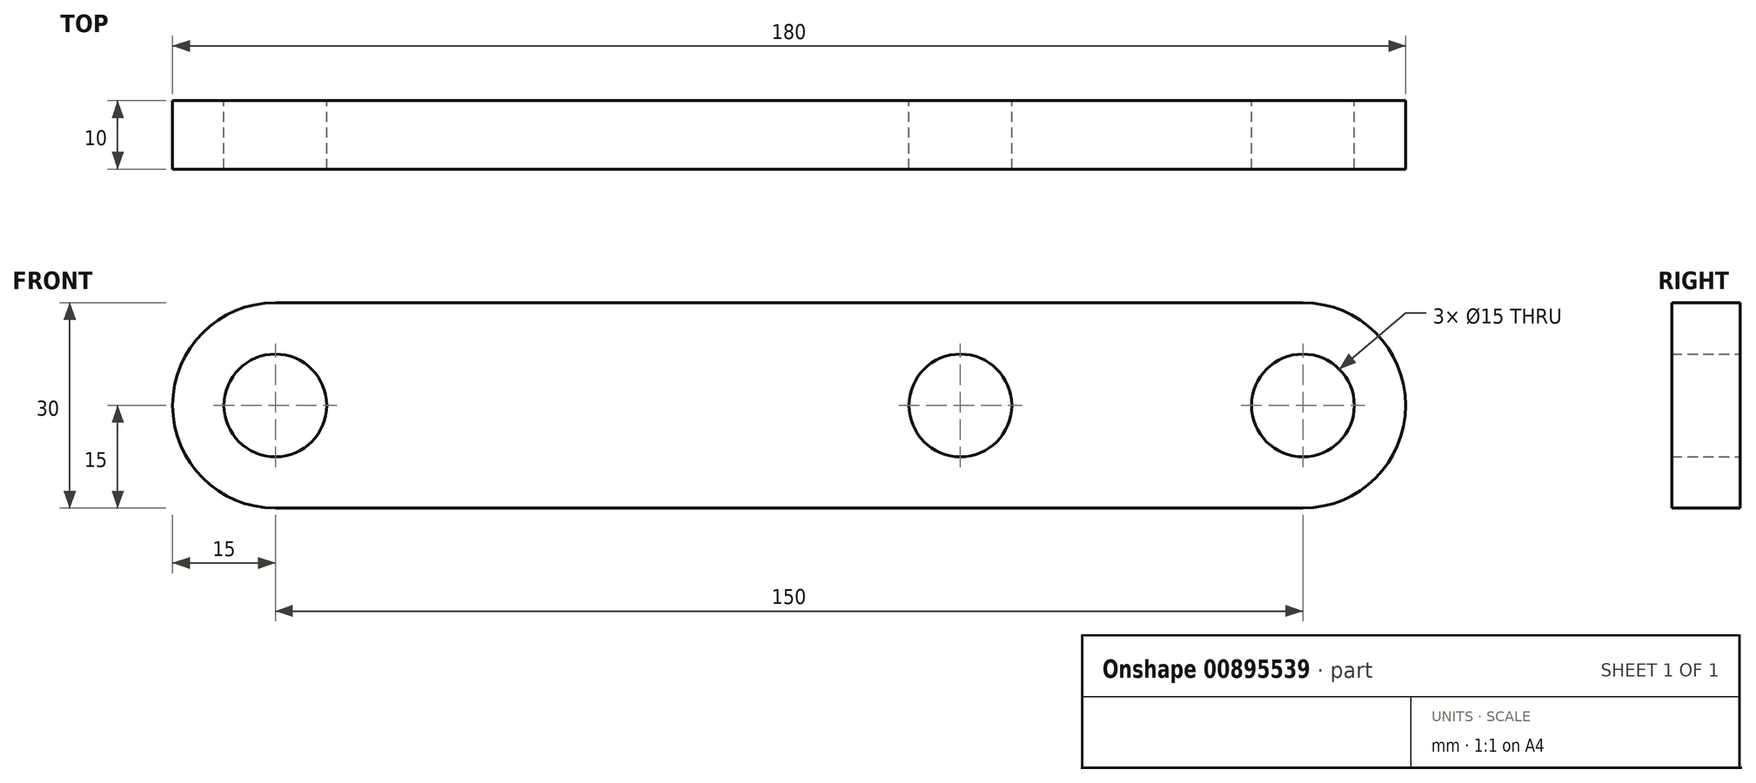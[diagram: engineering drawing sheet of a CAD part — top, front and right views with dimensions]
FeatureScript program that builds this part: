
annotation { "Feature Type Name" : "Feature", "Feature Type Description" : "" }
export const myFeature = defineFeature(function(context is Context, id is Id, definition is map)
    precondition{}
    {
        {
            var Q0;
            Q0=qCreatedBy(makeId("Front.planeOp"),FACE);
            var sketch = newSketch(context, id + "F0", { "sketchPlane" : qUnion([Q0])});
            skCircle(sketch, "E0", {"center": v(0, 0) * mm, "radius": 7.5 * mm});
            skArc(sketch, "E1", {"start": v(0, 15) * mm, "mid": v(-15, 0) * mm, "end": v(0, -15) * mm});
            skCircle(sketch, "E2", {"center": v(150, 0) * mm, "radius": 7.5 * mm});
            skArc(sketch, "E3", {"start": v(150, -15) * mm, "mid": v(165, 0) * mm, "end": v(150, 15) * mm});
            skLineSegment(sketch, "E4", {"start": v(0, 15) * mm, "end": v(150, 15) * mm});
            skLineSegment(sketch, "E5", {"start": v(0, -15) * mm, "end": v(150, -15) * mm});
            skCircle(sketch, "E6", {"center": v(100, 0) * mm, "radius": 7.5 * mm});
            skSolve(sketch);
        }
        {
            var Q0;
            Q0=makeQuery(id+"F0.imprint","IMPRINT",FACE,{"disambiguationData":[TD([[makeQuery(id+"F0.imprint","IMPRINT",EDGE,{"derivedFrom":sQuery(id+"F0.wireOp",EDGE,"E0")}),-1.0]])]});
            extrude(context, id + "F1", {"entities" : qUnion([Q0]), "depth" : 10 * mm, "offsetDistance" : 25 * mm});
        }
    });
